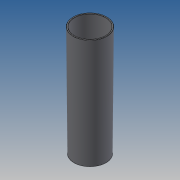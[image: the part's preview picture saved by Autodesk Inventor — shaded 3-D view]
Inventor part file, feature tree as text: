
AUTODESK INVENTOR PART (.ipt)
format: ipt  version: 2018.3 (Build 223284000, 284)  size: 133,120 bytes
history: native  units: in
note: dims shown in document units (in); Inventor stores cm internally (conversion verified against a paired STEP export)
features: revolve x1, fillet x1, sketch x1
ambient origin geometry x8: Origin, YZ Plane, XZ Plane, XY Plane, X Axis, Y Axis, Z Axis, Center Point
bodies: Solid1 (feature_tree)
feature tree (3):
  revolve  "Revolution1"  [1 undecoded]
  fillet  "Fillet1"  Radius=3.699in
  sketch  "Sketch1"  dims[d0=1.072in d1=1.13in d2=3.699in d3=0.043in d5=0.033in d6=0.043in d7=90.0deg d8=0.01in d9=1.044in]
note: 1 required parameter value undecoded (feature->parameter linkage not recoverable at this tier; creation-order binding heuristic only, values carry confidence <= 0.55)
